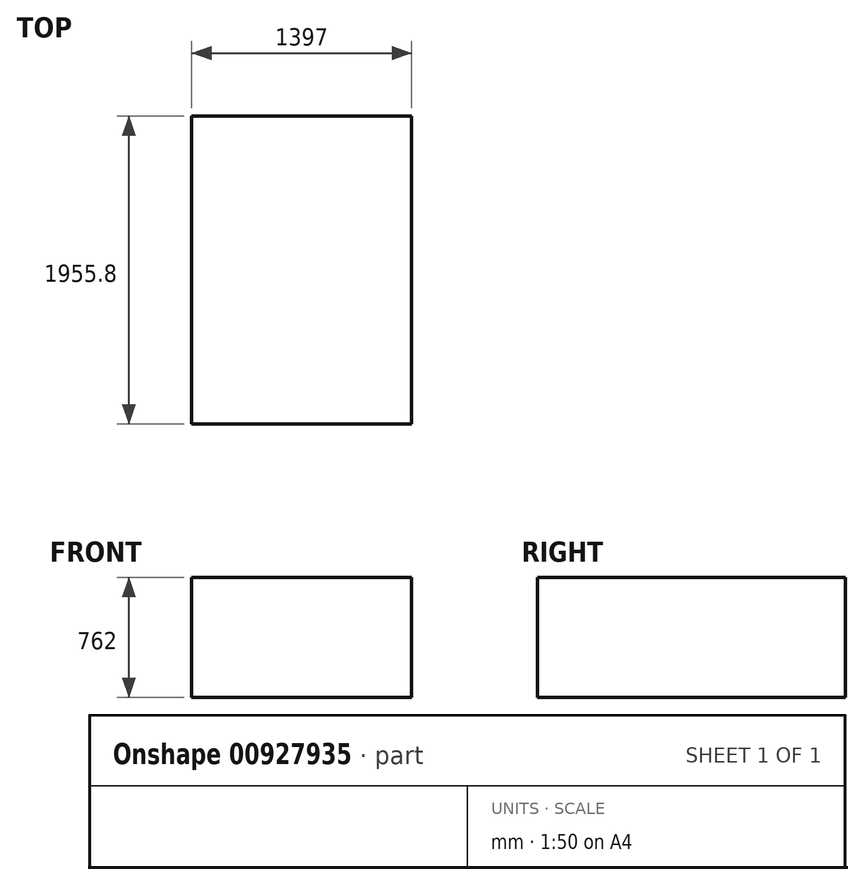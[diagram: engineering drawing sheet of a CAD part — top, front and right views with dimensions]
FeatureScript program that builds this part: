
annotation { "Feature Type Name" : "Feature", "Feature Type Description" : "" }
export const myFeature = defineFeature(function(context is Context, id is Id, definition is map)
    precondition{}
    {
        {
            var Q0;
            Q0=qCreatedBy(makeId("Top.planeOp"),FACE);
            var sketch = newSketch(context, id + "F0", { "sketchPlane" : qUnion([Q0])});
            skLineSegment(sketch, "E0.bottom", {"start": v(698.5, -986.03) * mm, "end": v(-698.5, -986.03) * mm});
            skLineSegment(sketch, "E0.top", {"start": v(698.5, 969.77) * mm, "end": v(-698.5, 969.77) * mm});
            skLineSegment(sketch, "E0.left", {"start": v(698.5, -986.03) * mm, "end": v(698.5, 969.77) * mm});
            skLineSegment(sketch, "E0.right", {"start": v(-698.5, -986.03) * mm, "end": v(-698.5, 969.77) * mm});
            skPoint(sketch, "E0.middle", {"position": v(0, -8.13) * mm});
            skSolve(sketch);
        }
        {
            var Q0;
            Q0 = qSketchRegion(id + "F0", true);
            extrude(context, id + "F1", {"entities" : qUnion([Q0]), "depth" : 762 * mm, "offsetDistance" : 25.4 * mm});
        }
    });
